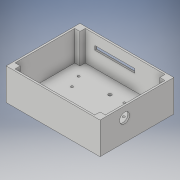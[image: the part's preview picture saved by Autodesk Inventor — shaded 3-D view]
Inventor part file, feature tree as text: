
AUTODESK INVENTOR PART (.ipt)
format: ipt  version: 2018 (Build 220112000, 112)  size: 172,032 bytes
history: native  units: in
note: dims shown in document units (in); Inventor stores cm internally (conversion verified against a paired STEP export)
features: extrude x6, sketch x6
ambient origin geometry x8: Origin, YZ Plane, XZ Plane, XY Plane, X Axis, Y Axis, Z Axis, Center Point
bodies: Solid1 (feature_tree)
feature tree (12):
  extrude  "Extrusion1"  Depth=3.701in
  extrude  "Extrusion2"  Depth=4.527in
  extrude  "Extrusion3"  Depth=0.354in
  extrude  "Extrusion4"  Depth=0.354in
  extrude  "Extrusion5"  Depth=1.5in TaperAngle=0.0deg
  extrude  "Extrusion6"  Depth=1.0in
  sketch  "Sketch1"  dims[d0=4.705in d1=3.701in]
  sketch  "Sketch2"  dims[d2=0.089in d3=0.0in d4=4.527in]
  sketch  "Sketch3"  dims[d5=3.523in d6=0.354in]
  sketch  "Sketch4"  dims[d7=0.354in d10=0.354in]
  sketch  "Sketch6"  dims[d11=0.354in d14=1.5in d15=0.0in]
  sketch  "Sketch7"  dims[d18=0.164in d19=0.164in d20=0.0in d21=0.0in d22=3.42in d23=2.271in d25=0.787in d30=0.112in d31=0.112in d36=0.112in d37=0.112in d38=0.118in d39=0.118in d40=0.118in d41=0.118in d42=0.0in d43=0.0in d44=0.5in d45=1.5in d46=0.0in d47=2.0in d48=1.0in d49=0.0in]
